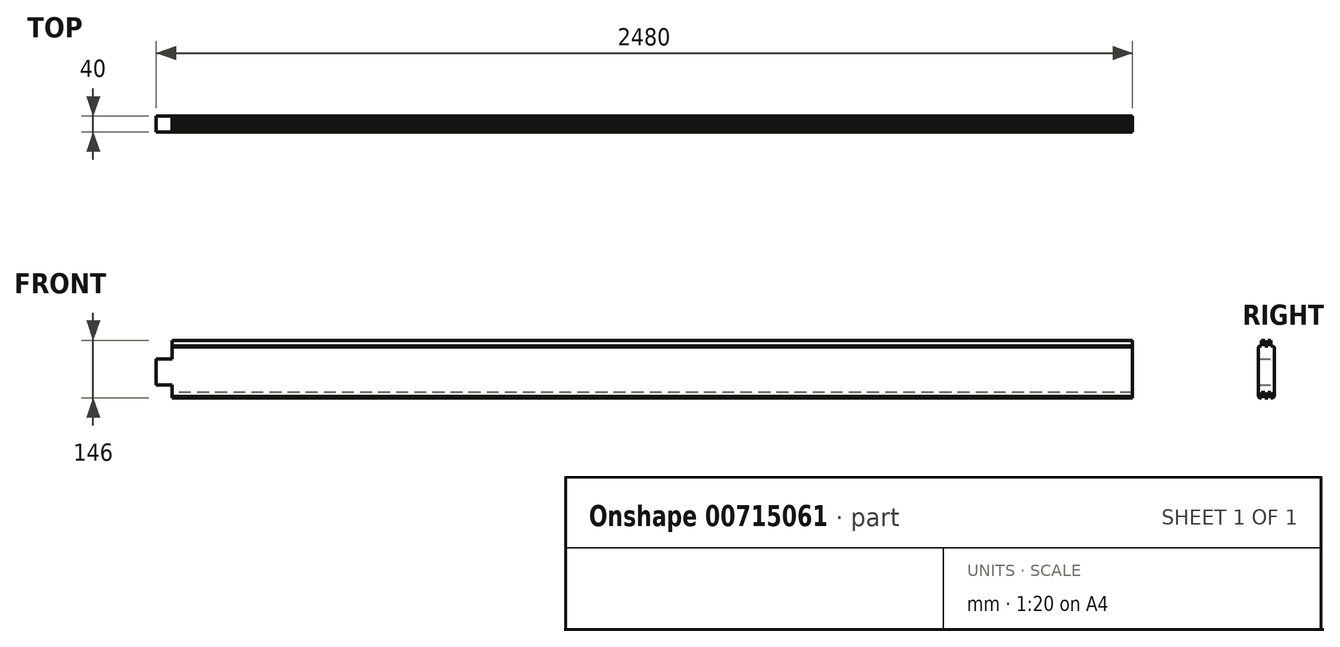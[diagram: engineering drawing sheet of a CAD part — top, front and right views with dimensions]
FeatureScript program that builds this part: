
annotation { "Feature Type Name" : "Feature", "Feature Type Description" : "" }
export const myFeature = defineFeature(function(context is Context, id is Id, definition is map)
    precondition{}
    {
        {
            assignVariable(context, id + "F0", {"name" : "Laenge", "anyValue" : 5100 - 1200 - 1420});
        }
        {
            var Q0;
            Q0=qCreatedBy(makeId("Right.planeOp"),FACE);
            var sketch = newSketch(context, id + "F1", { "sketchPlane" : qUnion([Q0])});
            skLineSegment(sketch, "E0", {"start": v(20, 63) * mm, "end": v(20, -63) * mm});
            skLineSegment(sketch, "E1", {"start": v(20, -63) * mm, "end": v(17, -66) * mm});
            skLineSegment(sketch, "E2", {"start": v(17, -66) * mm, "end": v(12, -66) * mm});
            skLineSegment(sketch, "E3", {"start": v(12, -52) * mm, "end": v(12, -66) * mm});
            skLineSegment(sketch, "E4", {"start": v(12, -52) * mm, "end": v(4, -52) * mm});
            skLineSegment(sketch, "E5", {"start": v(4, -66) * mm, "end": v(4, -52) * mm});
            skLineSegment(sketch, "E6", {"start": v(4, -66) * mm, "end": v(-4, -66) * mm});
            skLineSegment(sketch, "E7", {"start": v(-4, -52) * mm, "end": v(-4, -66) * mm});
            skLineSegment(sketch, "E8", {"start": v(-4, -52) * mm, "end": v(-12, -52) * mm});
            skLineSegment(sketch, "E9", {"start": v(-12, -66) * mm, "end": v(-12, -52) * mm});
            skLineSegment(sketch, "E10", {"start": v(-12, -66) * mm, "end": v(-17, -66) * mm});
            skLineSegment(sketch, "E11", {"start": v(-17, -66) * mm, "end": v(-20, -63) * mm});
            skLineSegment(sketch, "E12", {"start": v(-20, -63) * mm, "end": v(-20, 63) * mm});
            skLineSegment(sketch, "E13", {"start": v(-20, 63) * mm, "end": v(-17, 66) * mm});
            skLineSegment(sketch, "E14", {"start": v(-17, 66) * mm, "end": v(-12, 66) * mm});
            skLineSegment(sketch, "E15", {"start": v(-4, 66) * mm, "end": v(4, 66) * mm});
            skLineSegment(sketch, "E16", {"start": v(12, 66) * mm, "end": v(17, 66) * mm});
            skLineSegment(sketch, "E17", {"start": v(17, 66) * mm, "end": v(20, 63) * mm});
            skPoint(sketch, "E18.end.orphan", {"position": v(12, 57.8) * mm});
            skPoint(sketch, "E19.end.orphan", {"position": v(4, 66.3) * mm});
            skPoint(sketch, "E20.end.orphan", {"position": v(-4, 66.3) * mm});
            skLineSegment(sketch, "E21", {"start": v(-12, 66) * mm, "end": v(-12, 80) * mm});
            skLineSegment(sketch, "E22", {"start": v(-12, 80) * mm, "end": v(-4, 80) * mm});
            skLineSegment(sketch, "E23", {"start": v(-4, 80) * mm, "end": v(-4, 66) * mm});
            skLineSegment(sketch, "E24", {"start": v(4, 66) * mm, "end": v(4, 80) * mm});
            skLineSegment(sketch, "E25", {"start": v(4, 80) * mm, "end": v(12, 80) * mm});
            skLineSegment(sketch, "E26", {"start": v(12, 80) * mm, "end": v(12, 66) * mm});
            skLineSegment(sketch, "E27", {"start": v(20, -33) * mm, "end": v(-20, -33) * mm});
            skLineSegment(sketch, "E28", {"start": v(20, 33) * mm, "end": v(-20, 33) * mm});
            skPoint(sketch, "E29.end.orphan", {"position": v(-141.42, 0) * mm});
            skLineSegment(sketch, "E30", {"start": v(20, 0) * mm, "end": v(-20, 0) * mm});
            skLineSegment(sketch, "E31", {"start": v(20, 0) * mm, "end": v(-20, 0) * mm, "construction": true});
            skLineSegment(sketch, "E32", {"start": v(0, 33) * mm, "end": v(0, -33) * mm, "construction": true});
            skLineSegment(sketch, "E33", {"start": v(20, -52) * mm, "end": v(-20, -52) * mm});
            skSolve(sketch);
        }
        {
            var Q0;
            Q0=qCreatedBy(makeId("Front.planeOp"),FACE);
            var sketch = newSketch(context, id + "F2", { "sketchPlane" : qUnion([Q0])});
            skLineSegment(sketch, "E34", {"start": v(1240, 0) * mm, "end": v(-1240, 0) * mm, "construction": true});
            skPoint(sketch, "E35.right.start.orphan", {"position": v(-259.12, 108.1) * mm});
            skPoint(sketch, "E36.left.start.orphan", {"position": v(237.35, 108.1) * mm});
            skPoint(sketch, "E37.left.end.orphan", {"position": v(237.35, -84.05) * mm});
            skPoint(sketch, "E37.bottom.start.orphan", {"position": v(237.35, -117.05) * mm});
            skPoint(sketch, "E38.right.start.orphan", {"position": v(-259.12, -117.05) * mm});
            skPoint(sketch, "E38.top.end.orphan", {"position": v(-259.12, -84.05) * mm});
            skLineSegment(sketch, "E39.bottom", {"start": v(-1280, 33) * mm, "end": v(-1200, 33) * mm});
            skLineSegment(sketch, "E39.top", {"start": v(-1280, 133) * mm, "end": v(-1200, 133) * mm});
            skLineSegment(sketch, "E39.left", {"start": v(-1280, 33) * mm, "end": v(-1280, 133) * mm});
            skLineSegment(sketch, "E39.right", {"start": v(-1200, 33) * mm, "end": v(-1200, 133) * mm});
            skPoint(sketch, "E39.middle", {"position": v(-1240, 83) * mm});
            skLineSegment(sketch, "E40.bottom", {"start": v(-1280, -133) * mm, "end": v(-1200, -133) * mm});
            skLineSegment(sketch, "E40.top", {"start": v(-1280, -33) * mm, "end": v(-1200, -33) * mm});
            skLineSegment(sketch, "E40.left", {"start": v(-1280, -133) * mm, "end": v(-1280, -33) * mm});
            skLineSegment(sketch, "E40.right", {"start": v(-1200, -133) * mm, "end": v(-1200, -33) * mm});
            skPoint(sketch, "E40.middle", {"position": v(-1240, -83) * mm});
            skLineSegment(sketch, "E41.bottom", {"start": v(1280, 33) * mm, "end": v(1200, 33) * mm});
            skLineSegment(sketch, "E41.top", {"start": v(1280, 133) * mm, "end": v(1200, 133) * mm});
            skLineSegment(sketch, "E41.left", {"start": v(1280, 33) * mm, "end": v(1280, 133) * mm});
            skLineSegment(sketch, "E41.right", {"start": v(1200, 33) * mm, "end": v(1200, 133) * mm});
            skPoint(sketch, "E41.middle", {"position": v(1240, 83) * mm});
            skLineSegment(sketch, "E42.bottom", {"start": v(1280, -33) * mm, "end": v(1200, -33) * mm});
            skLineSegment(sketch, "E42.top", {"start": v(1280, -133) * mm, "end": v(1200, -133) * mm});
            skLineSegment(sketch, "E42.left", {"start": v(1280, -33) * mm, "end": v(1280, -133) * mm});
            skLineSegment(sketch, "E42.right", {"start": v(1200, -33) * mm, "end": v(1200, -133) * mm});
            skPoint(sketch, "E42.middle", {"position": v(1240, -83) * mm});
            skSolve(sketch);
        }
        {
            var Q0;
            {var subQ3=sQuery(id+"F1.wireOp",EDGE,"E13");Q0=makeQuery(id+"F1.imprint","IMPRINT",FACE,{"disambiguationData":[TD([[makeQuery(id+"F1.imprint","IMPRINT",EDGE,{"derivedFrom":subQ3}),-1.0]])]});}
            var Q1;
            {var subQ0=sQuery(id+"F1.wireOp",EDGE,"E28");Q1=makeQuery(id+"F1.imprint","IMPRINT",FACE,{"disambiguationData":[TD([[makeQuery(id+"F1.imprint","IMPRINT",EDGE,{"derivedFrom":subQ0}),1.0]])]});}
            var Q2;
            {var subQ0=sQuery(id+"F1.wireOp",EDGE,"E27");Q2=makeQuery(id+"F1.imprint","IMPRINT",FACE,{"disambiguationData":[TD([[makeQuery(id+"F1.imprint","IMPRINT",EDGE,{"derivedFrom":subQ0}),-1.0]])]});}
            var Q3;
            {var subQ0=sQuery(id+"F1.wireOp",EDGE,"E27");Q3=makeQuery(id+"F1.imprint","IMPRINT",FACE,{"disambiguationData":[TD([[makeQuery(id+"F1.imprint","IMPRINT",EDGE,{"derivedFrom":subQ0}),1.0]])]});}
            var Q4;
            {var subQ4=sQuery(id+"F1.wireOp",EDGE,"E9");Q4=makeQuery(id+"F1.imprint","IMPRINT",FACE,{"disambiguationData":[TD([[makeQuery(id+"F1.imprint","IMPRINT",EDGE,{"derivedFrom":subQ4}),1.0]])]});}
            var Q5;
            {var subQ0=sQuery(id+"F1.wireOp",EDGE,"E5");Q5=makeQuery(id+"F1.imprint","IMPRINT",FACE,{"disambiguationData":[TD([[makeQuery(id+"F1.imprint","IMPRINT",EDGE,{"derivedFrom":subQ0}),1.0]])]});}
            var Q6;
            {var subQ1=sQuery(id+"F1.wireOp",EDGE,"E1");Q6=makeQuery(id+"F1.imprint","IMPRINT",FACE,{"disambiguationData":[TD([[makeQuery(id+"F1.imprint","IMPRINT",EDGE,{"derivedFrom":subQ1}),-1.0]])]});}
            extrude(context, id + "F3", {"entities" : qUnion([Q0, Q1, Q2, Q3, Q4, Q5, Q6]), "endBound" : BoundingType.SYMMETRIC, "depth" : getVariable(context, 'Laenge') * mm, "offsetDistance" : 25 * mm});
        }
        {
            var Q0;
            Q0=makeQuery(id+"F2.imprint","IMPRINT",FACE,{"disambiguationData":[TD([[makeQuery(id+"F2.imprint","IMPRINT",EDGE,{"derivedFrom":sQuery(id+"F2.wireOp",EDGE,"E39.bottom")}),1.0]])]});
            var Q1;
            Q1=makeQuery(id+"F2.imprint","IMPRINT",FACE,{"disambiguationData":[TD([[makeQuery(id+"F2.imprint","IMPRINT",EDGE,{"derivedFrom":sQuery(id+"F2.wireOp",EDGE,"E40.bottom")}),1.0]])]});
            extrude(context, id + "F4", {"entities" : qUnion([Q0, Q1]), "operationType" : NewBodyOperationType.REMOVE, "endBound" : BoundingType.SYMMETRIC, "oppositeDirection" : true, "depth" : 50 * mm, "offsetDistance" : 25 * mm});
        }
    });
